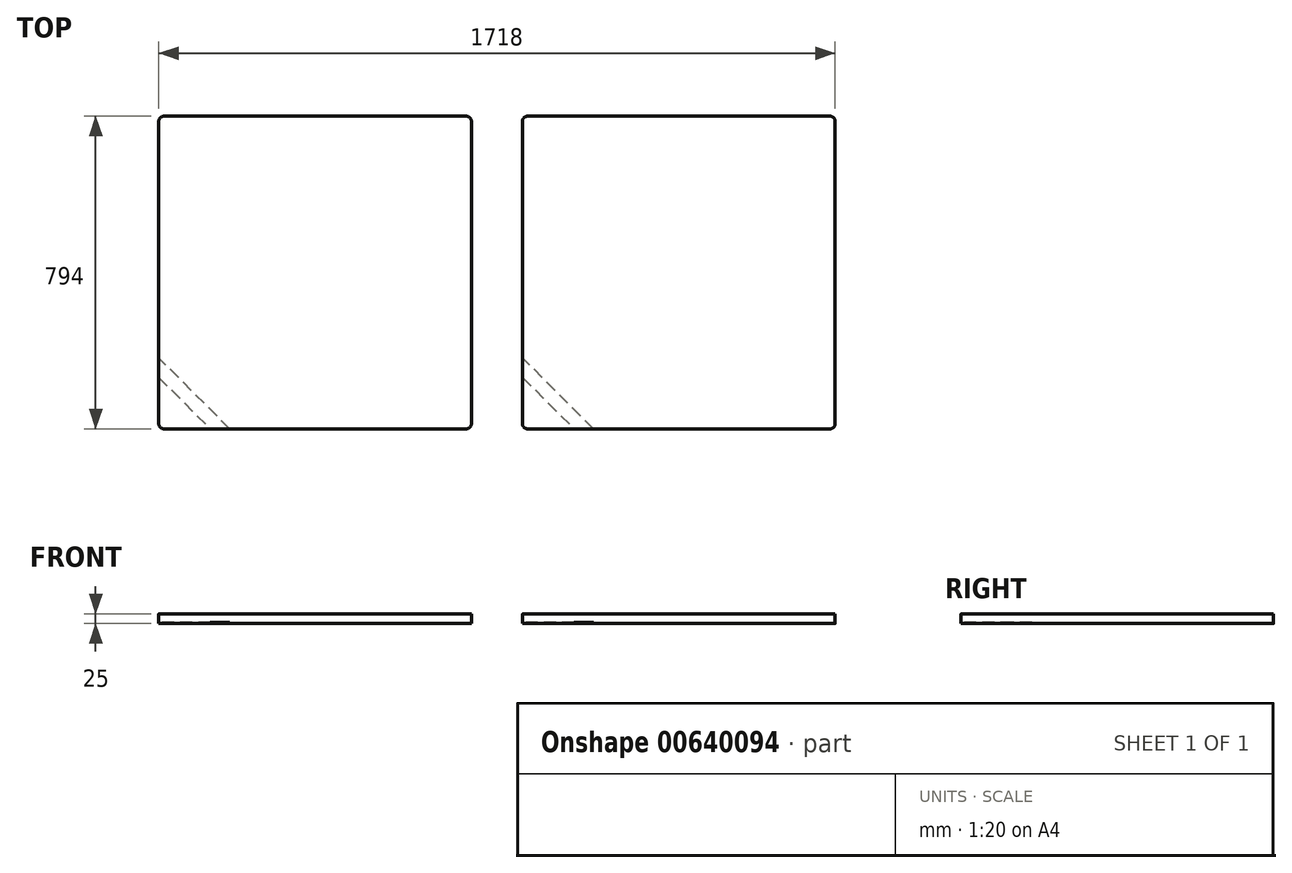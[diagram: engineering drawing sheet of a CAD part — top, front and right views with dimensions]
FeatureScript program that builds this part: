
annotation { "Feature Type Name" : "Feature", "Feature Type Description" : "" }
export const myFeature = defineFeature(function(context is Context, id is Id, definition is map)
    precondition{}
    {
        {
            var Q0;
            Q0=qCreatedBy(makeId("Top.planeOp"),FACE);
            var sketch = newSketch(context, id + "F0", { "sketchPlane" : qUnion([Q0])});
            skLineSegment(sketch, "E0.bottom", {"start": v(385, 397) * mm, "end": v(-385, 397) * mm});
            skLineSegment(sketch, "E0.top", {"start": v(385, -397) * mm, "end": v(-385, -397) * mm});
            skLineSegment(sketch, "E0.left", {"start": v(397, 385) * mm, "end": v(397, -385) * mm});
            skLineSegment(sketch, "E0.right", {"start": v(-397, 385) * mm, "end": v(-397, -385) * mm});
            skPoint(sketch, "E0.middle", {"position": v(0, 0) * mm});
            skPoint(sketch, "E1.visualSharp", {"position": v(-397, 397) * mm});
            skArc(sketch, "E1.filletArc", {"start": v(-385, 397) * mm, "mid": v(-393.49, 393.49) * mm, "end": v(-397, 385) * mm});
            skPoint(sketch, "E2.visualSharp", {"position": v(-397, -397) * mm});
            skArc(sketch, "E2.filletArc", {"start": v(-397, -385) * mm, "mid": v(-393.49, -393.49) * mm, "end": v(-385, -397) * mm});
            skPoint(sketch, "E3.visualSharp", {"position": v(397, -397) * mm});
            skArc(sketch, "E3.filletArc", {"start": v(385, -397) * mm, "mid": v(393.49, -393.49) * mm, "end": v(397, -385) * mm});
            skPoint(sketch, "E4.visualSharp", {"position": v(397, 397) * mm});
            skArc(sketch, "E4.filletArc", {"start": v(397, 385) * mm, "mid": v(393.49, 393.49) * mm, "end": v(385, 397) * mm});
            skSolve(sketch);
        }
        {
            var Q0;
            Q0=qSketchRegion(id+"F0",true);
            extrude(context, id + "F1", {"entities" : qUnion([Q0]), "depth" : 25 * mm, "offsetDistance" : 25 * mm});
        }
        {
            var Q0;
            Q0=makeQuery(id+"F1.opExtrude","CAP_FACE",FACE,{"disambiguationData":[OSD([sQuery(id+"F0.wireOp",EDGE,"E0.bottom"),sQuery(id+"F0.wireOp",EDGE,"E0.top"),sQuery(id+"F0.wireOp",EDGE,"E0.left"),sQuery(id+"F0.wireOp",EDGE,"E0.right"),sQuery(id+"F0.wireOp",EDGE,"E1.filletArc"),sQuery(id+"F0.wireOp",EDGE,"E2.filletArc"),sQuery(id+"F0.wireOp",EDGE,"E3.filletArc"),sQuery(id+"F0.wireOp",EDGE,"E4.filletArc")])],"isStart":true});
            var sketch = newSketch(context, id + "F2", { "sketchPlane" : qUnion([Q0])});
            skLineSegment(sketch, "E5", {"start": v(397, 397) * mm, "end": v(-397, -397) * mm, "construction": true});
            skLineSegment(sketch, "E6", {"start": v(-266.5, 397) * mm, "end": v(-217, 397) * mm});
            skLineSegment(sketch, "E7", {"start": v(-217, 397) * mm, "end": v(-397, 217) * mm});
            skLineSegment(sketch, "E8", {"start": v(-397, 217) * mm, "end": v(-397, 266.5) * mm});
            skLineSegment(sketch, "E9", {"start": v(-397, 266.5) * mm, "end": v(-266.5, 397) * mm});
            skSolve(sketch);
        }
        {
            var Q0;
            Q0=sQuery(id+"F2.wireOp",EDGE,"E5");
            cPlane(context, id + "F3", {"entities" : qUnion([Q0]), "cplaneType" : CPlaneType.LINE_ANGLE, "offset" : 25 * mm, "angle" : 90 * degree, "width" : 150 * mm, "height" : 150 * mm});
        }
        {
            var Q0;
            Q0=qSketchRegion(id+"F2",true);
            extrude(context, id + "F4", {"entities" : qUnion([Q0]), "operationType" : NewBodyOperationType.REMOVE, "oppositeDirection" : true, "depth" : 3 * mm, "offsetDistance" : 25 * mm});
        }
        {
            var Q0;
            Q0=makeQuery(id+"F1.opExtrude","SWEPT_BODY",BODY,{"disambiguationData":[OSD([sQuery(id+"F0.wireOp",EDGE,"E0.bottom"),sQuery(id+"F0.wireOp",EDGE,"E0.top"),sQuery(id+"F0.wireOp",EDGE,"E0.left"),sQuery(id+"F0.wireOp",EDGE,"E0.right"),sQuery(id+"F0.wireOp",EDGE,"E1.filletArc"),sQuery(id+"F0.wireOp",EDGE,"E2.filletArc"),sQuery(id+"F0.wireOp",EDGE,"E3.filletArc"),sQuery(id+"F0.wireOp",EDGE,"E4.filletArc")])]});
            transform(context, id + "F5", {"entities" : qUnion([Q0]), "transformType" : TransformType.TRANSLATION_3D, "dx" : 924 * mm, "dy" : 0 * mm, "dz" : 0 * mm, "makeCopy" : true});
        }
    });
